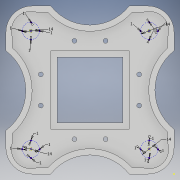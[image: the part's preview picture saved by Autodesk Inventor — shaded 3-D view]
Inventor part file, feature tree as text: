
AUTODESK INVENTOR PART (.ipt)
format: ipt  version: 2019 (Build 230136000, 136)  size: 346,112 bytes
history: native  units: mm
features: extrude x7, sketch x7, other x1, shell x1
ambient origin geometry x8: Origin, YZ Plane, XZ Plane, XY Plane, X Axis, Y Axis, Z Axis, Center Point
bodies: Body1 (feature_tree)
feature tree (16):
  other  "Твердое тело1"
  extrude  "Выдавливание1"  Depth=135.0mm
  extrude  "Выдавливание2"  Depth=135.0mm
  extrude  "Выдавливание3"  Depth=20.0mm
  extrude  "Выдавливание4"  Depth=20.0mm
  shell  "Оболочка1"  Thickness=20.0mm
  sketch  "Эскиз5"
  extrude  "Выдавливание6"  Depth=20.0mm
  extrude  "Выдавливание7"  Depth=21.5mm
  extrude  "Выдавливание8"  Depth=21.5mm
  sketch  "Эскиз1"
  sketch  "Эскиз2"
  sketch  "Эскиз3"
  sketch  "Эскиз4"
  sketch  "Эскиз6"
  sketch  "Эскиз7"
